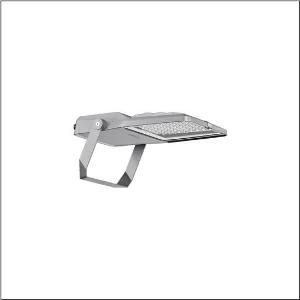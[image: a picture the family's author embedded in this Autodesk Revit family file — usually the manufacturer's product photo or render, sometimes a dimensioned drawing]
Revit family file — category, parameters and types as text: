
# Revit family: floodlight_fl_21_iq_mini___pl61_5xa7771d2c1a_1090
name_source: partatom
category: Lighting Fixtures
units: mm (PartAtom-declared; Revit-internal decimal feet)

## family parameters
Cut with Voids When Loaded = No
Host = Face
Light Source = No
Part Type = Normal
Room Calculation Point = No
Round Connector Dimension = Use Diameter
Shared = No

## types (1)
- --- (1 x LED, 17500 lm, 143 W, 3000K)
    Apparent Load = 143 VA
    CIE Flux Codes = 33 65 98 100 100
    Color Rendering = 70
    Color Temperature = 3000K
    Default Elevation = 1800 mm
    Description = Floodlight FL 21 iQ mini, floodlight, primary light control with lens, of PMMA, primary optical cover: protective disc, of toughened safety glass, transparent, light distribution: PL61, light emission: direct distribution, installation type: surface-mounted, lamps: LED, High Power LED, rated values: 17.500lm | 143W | 122,4lm/W (begin service life); end service life: 17.500lm | 151,6W; at 50% lumin. flux: 8.750lm | 60,6W | 144,4lm/W, colour temperature: 3000K, colour rendering: CRI > 70, light colour: 730, light setting 1 begin service life: 100% | 17.500lm | 143W | 122,4lm/W | 3.000K, light setting 1 end service life: 151,6W, further light settings possible, control: Auto-Match, Temp-Guard, Lumen-Switch, Night-Set, Smart-Wire, Light-Fading, Desk-Remote (wireless, voltage-free reading and setting of iQ features in the workshop via application-optimized NFC function/RFID function), optimised constant luminous flux control (CLO 2.0), pre-setting: linear dimming characteristic, with terminal, 6-pole, mains connection: 220..240V, AC, 50/60Hz, luminaire housing, of diecast aluminium, powder-coated, SITECO metallic grey (DB 702S), corrosivity category C5 mid according to DIN EN ISO 12944suitable for swimming poolschlorine-resistant, sealing non-destructively replaceable, mounting bracket, of steel, galvanised, powder-coated, SITECO metallic grey (DB 702S), protection rating (complete): IP66, insulation class (complete): insulation class II (safety insulation), certification: CE, ENEC, VDE, protection symbol: D, impact resistance: IK08, permissible operating ambient temperature: -40..+40°C, permissible operating ambient temperature for outdoor applications: -40..+50°C, standard: DIN EN 12944, LABS conformity tested according to VDMA 24364:2018-05, packaging unit: 1 piece

Light Distribution: PL61
    Height = 70 mm
    Lamp = 1 x LED
    Lamp Light Flux = 17500 lm
    Lamp Power = 143 W
    Lamp count = 1
    Length = 485 mm
    Luminous efficacy = 122 lm/W
    Manufacturer = Siteco
    ModVariant = No
    Model = 5XA7771D2C1A
    Mounting Place = Pole
    Mounting Type = Pole annexe
    Number of Poles = 1
    OnlyDefault = Yes
    Power Factor = 1
    Product Name = Floodlight FL 21 iQ mini | PL61
    Product group = floodlight | pylon annexe
    ProductGroupID = 6201
    Protection Class = Protection class II
    Protection Degree = IP 66
    RLX_Detail_Level = 1
    RLX_Emergency_Light_Flux = 0 lm
    RLX_Emergency_Type = 0
    RLX_Emergency_Type_DB = No
    RlxData = <blob elided: 96881 chars, md5=1ef7e696>
    Socket = socket
    Standby Power = 0 W
    System Light Flux = 17500 lm
    System Power = 143 W
    Type Comments = factory setting: luminous flux: 100 % | dim-lin: 254 | 730 mA
    Type Image = l_1006845.jpg
    URL = http://relux.com
    VarID = @adj_173835
    Voltage = 0 V
    Weight = 0.00 kg
    Width = 337 mm

## geometry (parser evidence)
native form markers: Blend x4, Sweep x13
no freeform markers — native parametric forms only
